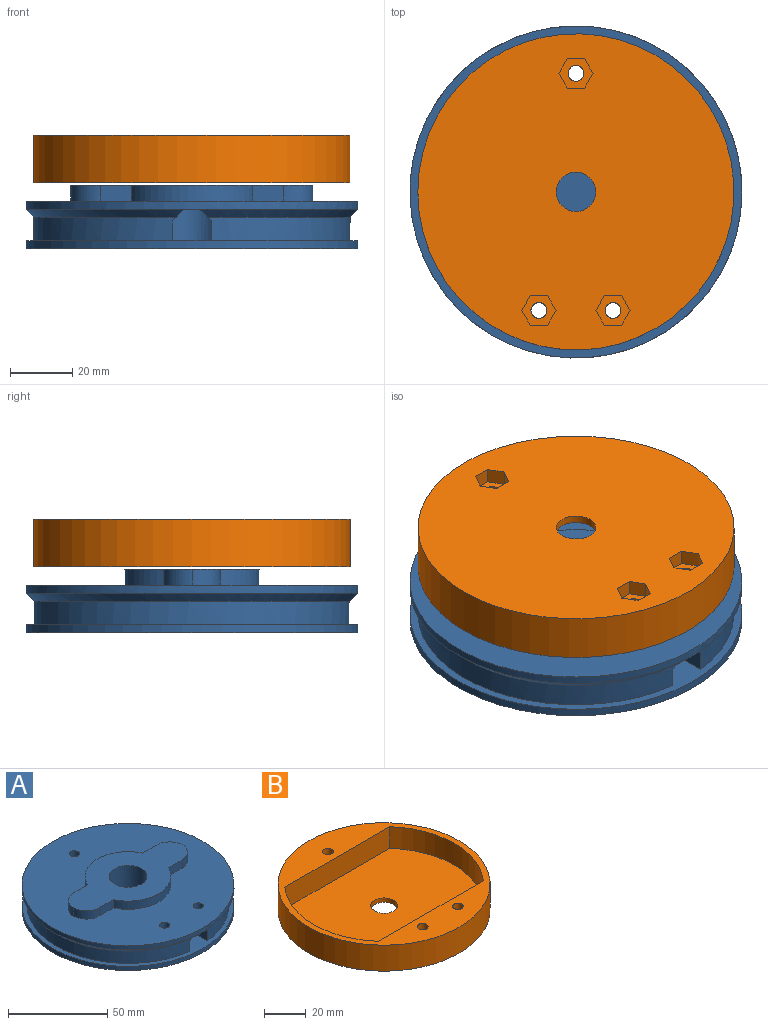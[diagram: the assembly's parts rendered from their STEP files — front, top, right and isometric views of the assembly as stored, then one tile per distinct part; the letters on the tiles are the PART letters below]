
ASSEMBLY  parts=2 mates=2
PART A: 33 faces, bbox 106.7x106.7x20.3 mm
  f0: plane 43.3x6.35mm, normal (-1,0,0), area 275mm2, adj f2,f10,f20,f22
  f1: plane 43.3x6.35mm, normal (1,0,0), area 275mm2, adj f2,f10,f20,f23
  f2: cylinder r=50.8mm len=101.6mm, axis (0,0,-1), area 2336.8mm2, adj f0,f1,f10,f21,f22,f23
  f3: plane 106.68x106.68mm, normal (0,0,1), area 6833.2mm2, adj f4,f5,f6,f12,f13,f14,f15,f16
  f4: cylinder r=21.59mm len=39.12mm, axis (0,0,-1), area 248.6mm2, adj f3,f11,f12,f14
  f5: cylinder r=21.59mm len=39.12mm, axis (0,0,-1), area 248.6mm2, adj f3,f11,f13,f15
  f6: cylinder r=53.34mm len=106.68mm, axis (0,0,-1), area 851.3mm2, adj f3,f7,f21
  f7: plane 44.16x5.08mm, normal (0,0,-1), area 223.1mm2, adj f6,f20,f22,f23
  f8: cylinder r=53.34mm len=106.68mm, axis (0,0,1), area 851.3mm2, adj f9,f10
  f9: plane 106.68x106.68mm, normal (0,0,-1), area 8724.6mm2, adj f8,f26,f29,f32
  f10: plane 106.68x106.68mm, normal (0,0,1), area 1648.2mm2, adj f0,f1,f2,f8,f20
  f11: plane 77.77x43.18mm, normal (0,0,1), area 1758.7mm2, adj f4,f5,f12,f13,f14,f15,f16,f17
  f12: plane 9.81x5.08mm, normal (0,1,0), area 49.8mm2, adj f3,f4,f11,f17
  f13: plane 9.81x5.08mm, normal (0,-1,0), area 49.8mm2, adj f3,f5,f11,f16
  f14: plane 9.81x5.08mm, normal (0,1,0), area 49.8mm2, adj f3,f4,f11,f19
  f15: plane 9.81x5.08mm, normal (0,-1,0), area 49.8mm2, adj f3,f5,f11,f18
  f16: cylinder r=9.53mm len=9.52mm, axis (0,0,1), area 74.1mm2, adj f3,f11,f13,f17
  f17: cylinder r=9.53mm len=9.52mm, axis (0,0,-1), area 74.1mm2, adj f3,f11,f12,f16
  f18: cylinder r=9.53mm len=9.52mm, axis (0,0,-1), area 74.1mm2, adj f3,f11,f15,f19
  f19: cylinder r=9.53mm len=9.52mm, axis (0,0,1), area 74.1mm2, adj f3,f11,f14,f18
  f20: cylinder r=9.53mm len=19.05mm, axis (0,0,-1), area 940.2mm2, adj f0,f1,f7,f10,f11,f22,f23
  f21: cone r=53.34mm half-angle=45deg, axis (0,0,1), area 1147.8mm2, adj f2,f6,f22,f23
  f22: plane 46.18x3.81mm, normal (-0.71,0,-0.71), area 232.3mm2, adj f0,f2,f7,f20,f21
  f23: plane 46.18x3.81mm, normal (0.71,0,-0.71), area 232.3mm2, adj f1,f2,f7,f20,f21
  f24: cylinder r=2.55mm len=10.41mm, axis (0,0,-1), area 167mm2, adj f3,f25
  f25: plane 9.53x9.53mm, normal (0,0,-1), area 50.8mm2, adj f24,f26
  f26: cylinder r=4.76mm len=9.53mm, axis (0,0,-1), area 144.4mm2, adj f9,f25
  f27: cylinder r=2.55mm len=10.41mm, axis (0,0,-1), area 167mm2, adj f3,f28
  f28: plane 9.53x9.53mm, normal (0,0,-1), area 50.8mm2, adj f27,f29
  f29: cylinder r=4.76mm len=9.53mm, axis (0,0,-1), area 144.4mm2, adj f9,f28
  f30: cylinder r=2.55mm len=10.41mm, axis (0,0,-1), area 167mm2, adj f3,f31
  f31: plane 9.53x9.53mm, normal (0,0,-1), area 50.8mm2, adj f30,f32
  f32: cylinder r=4.76mm len=9.53mm, axis (0,0,-1), area 144.4mm2, adj f9,f31
PART B: 33 faces, bbox 101.6x101.6x15.2 mm
  f0: plane 101.6x101.6mm, normal (0,0,-1), area 7744.9mm2, adj f1,f14,f15,f16,f17,f18,f19,f20
  f1: cylinder r=50.8mm len=101.6mm, axis (0,0,-1), area 4864.4mm2, adj f0,f2
  f2: plane 101.6x101.6mm, normal (0,0,1), area 2481.6mm2, adj f1,f3,f4,f5,f6,f8,f10,f12
  f3: plane 71x12.7mm, normal (0,-1,0), area 901.6mm2, adj f2,f5,f6,f7
  f4: plane 71x12.7mm, normal (0,1,0), area 901.6mm2, adj f2,f5,f6,f7
  f5: cylinder r=47.62mm len=63.5mm, axis (0,0,1), area 882.7mm2, adj f2,f3,f4,f7
  f6: cylinder r=47.62mm len=63.5mm, axis (0,0,1), area 882.7mm2, adj f2,f3,f4,f7
  f7: plane 95.25x63.5mm, normal (0,0,1), area 5437.7mm2, adj f3,f4,f5,f6,f32
  f8: cylinder r=2.55mm len=10.41mm, axis (0,0,-1), area 167mm2, adj f2,f9
  f9: plane 11x9.53mm, normal (0,0,-1), area 58.1mm2, adj f8,f26,f27,f28,f29,f30,f31
  f10: cylinder r=2.55mm len=10.41mm, axis (0,0,-1), area 167mm2, adj f2,f11
  f11: plane 11x9.53mm, normal (0,0,-1), area 58.1mm2, adj f10,f20,f21,f22,f23,f24,f25
  f12: cylinder r=2.55mm len=10.41mm, axis (0,0,-1), area 167mm2, adj f2,f13
  f13: plane 11x9.53mm, normal (0,0,-1), area 58.1mm2, adj f12,f14,f15,f16,f17,f18,f19
  f14: plane 5.5x4.83mm, normal (0,1,0), area 26.5mm2, adj f0,f13,f15,f17
  f15: plane 4.83x4.76mm, normal (0.87,0.5,0), area 26.5mm2, adj f0,f13,f14,f16
  f16: plane 4.83x4.76mm, normal (0.87,-0.5,0), area 26.5mm2, adj f0,f13,f15,f18
  f17: plane 4.83x4.76mm, normal (-0.87,0.5,0), area 26.5mm2, adj f0,f13,f14,f19
  f18: plane 5.5x4.83mm, normal (0,-1,0), area 26.5mm2, adj f0,f13,f16,f19
  f19: plane 4.83x4.76mm, normal (-0.87,-0.5,0), area 26.5mm2, adj f0,f13,f17,f18
  f20: plane 5.5x4.83mm, normal (0,1,0), area 26.5mm2, adj f0,f11,f21,f23
  f21: plane 4.83x4.76mm, normal (0.87,0.5,0), area 26.5mm2, adj f0,f11,f20,f22
  f22: plane 4.83x4.76mm, normal (0.87,-0.5,0), area 26.5mm2, adj f0,f11,f21,f24
  f23: plane 4.83x4.76mm, normal (-0.87,0.5,0), area 26.5mm2, adj f0,f11,f20,f25
  f24: plane 5.5x4.83mm, normal (0,-1,0), area 26.5mm2, adj f0,f11,f22,f25
  f25: plane 4.83x4.76mm, normal (-0.87,-0.5,0), area 26.5mm2, adj f0,f11,f23,f24
  f26: plane 5.5x4.83mm, normal (0,1,0), area 26.5mm2, adj f0,f9,f27,f29
  f27: plane 4.83x4.76mm, normal (0.87,0.5,0), area 26.5mm2, adj f0,f9,f26,f28
  f28: plane 4.83x4.76mm, normal (0.87,-0.5,0), area 26.5mm2, adj f0,f9,f27,f30
  f29: plane 4.83x4.76mm, normal (-0.87,0.5,0), area 26.5mm2, adj f0,f9,f26,f31
  f30: plane 5.5x4.83mm, normal (0,-1,0), area 26.5mm2, adj f0,f9,f28,f31
  f31: plane 4.83x4.76mm, normal (-0.87,-0.5,0), area 26.5mm2, adj f0,f9,f29,f30
  f32: cylinder r=6.35mm len=12.7mm, axis (0,0,-1), area 101.3mm2, adj f0,f7
PLACE A t=(-12.53,-57.9,45.72)mm fixed
PLACE B rot(axis=(0,1,0),180deg) t=(-12.53,-57.9,66.87)mm
MATE cylindrical B.f8 <-> A.f24  axis (0,0,1) through (-12.53,-19.8,69.66)mm
MATE cylindrical A.f27 <-> B.f12  axis (0,0,1) through (-0.63,-96,53.34)mm
